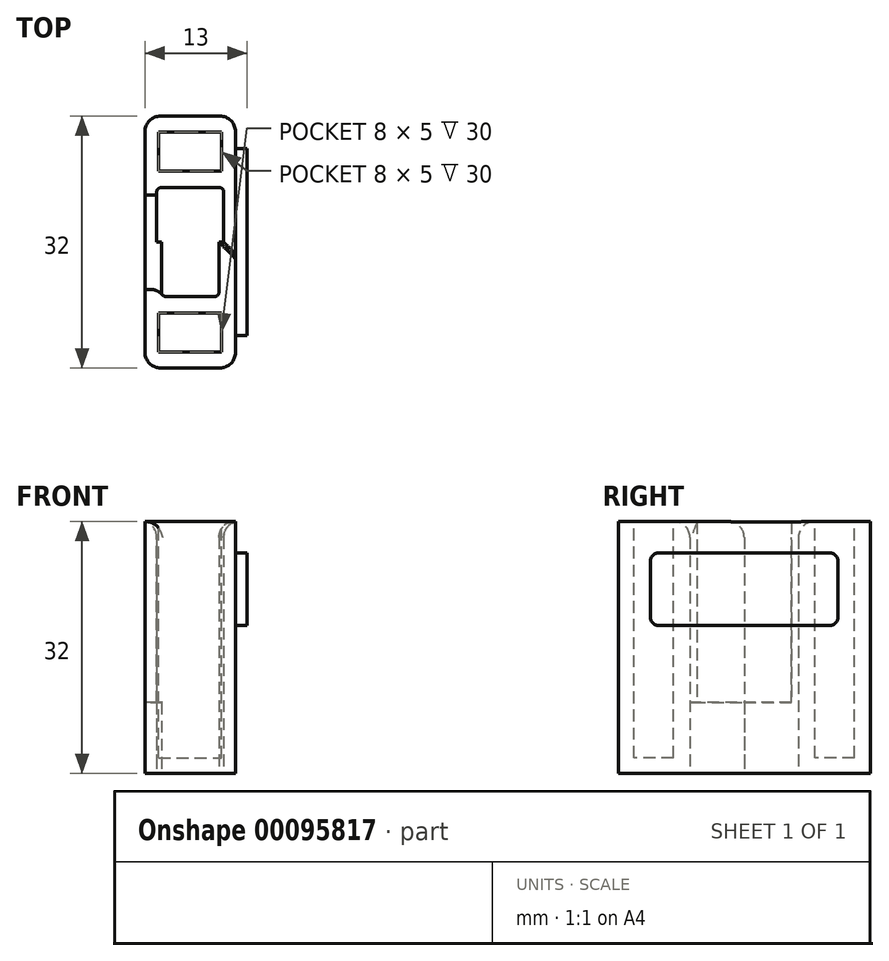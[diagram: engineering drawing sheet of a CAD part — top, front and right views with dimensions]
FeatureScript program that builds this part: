
annotation { "Feature Type Name" : "Feature", "Feature Type Description" : "" }
export const myFeature = defineFeature(function(context is Context, id is Id, definition is map)
    precondition{}
    {
        {
            var Q0;
            Q0=qCreatedBy(makeId("Top.planeOp"),FACE);
            var sketch = newSketch(context, id + "F0", { "sketchPlane" : qUnion([Q0])});
            skLineSegment(sketch, "E0.bottom", {"start": v(-3.75, 6.9) * mm, "end": v(3.75, 6.9) * mm});
            skLineSegment(sketch, "E0.left", {"start": v(-4.25, 6.4) * mm, "end": v(-4.25, 0) * mm});
            skLineSegment(sketch, "E0.right", {"start": v(4.25, 6.4) * mm, "end": v(4.25, 0) * mm});
            skLineSegment(sketch, "E1", {"start": v(-4.25, 0) * mm, "end": v(-3.65, 0) * mm});
            skLineSegment(sketch, "E2", {"start": v(-3.65, 0) * mm, "end": v(-3.65, -6.4) * mm});
            skLineSegment(sketch, "E3", {"start": v(4.25, 0) * mm, "end": v(3.65, 0) * mm});
            skLineSegment(sketch, "E4", {"start": v(3.65, 0) * mm, "end": v(3.65, -6.4) * mm});
            skLineSegment(sketch, "E5", {"start": v(-3.15, -6.9) * mm, "end": v(3.15, -6.9) * mm});
            skPoint(sketch, "E6.visualSharp", {"position": v(-4.25, 6.9) * mm});
            skArc(sketch, "E6.filletArc", {"start": v(-3.75, 6.9) * mm, "mid": v(-4.1, 6.75) * mm, "end": v(-4.25, 6.4) * mm});
            skPoint(sketch, "E7.visualSharp", {"position": v(4.25, 6.9) * mm});
            skArc(sketch, "E7.filletArc", {"start": v(4.25, 6.4) * mm, "mid": v(4.1, 6.75) * mm, "end": v(3.75, 6.9) * mm});
            skPoint(sketch, "E8.visualSharp", {"position": v(-3.65, -6.9) * mm});
            skArc(sketch, "E8.filletArc", {"start": v(-3.65, -6.4) * mm, "mid": v(-3.5, -6.75) * mm, "end": v(-3.15, -6.9) * mm});
            skPoint(sketch, "E9.visualSharp", {"position": v(3.65, -6.9) * mm});
            skArc(sketch, "E9.filletArc", {"start": v(3.15, -6.9) * mm, "mid": v(3.5, -6.75) * mm, "end": v(3.65, -6.4) * mm});
            skLineSegment(sketch, "E10.bottom", {"start": v(-5.75, 16) * mm, "end": v(5.75, 16) * mm});
            skLineSegment(sketch, "E10.top", {"start": v(-5.75, -16) * mm, "end": v(5.75, -16) * mm});
            skLineSegment(sketch, "E10.left", {"start": v(-5.75, 16) * mm, "end": v(-5.75, -16) * mm});
            skLineSegment(sketch, "E10.right", {"start": v(5.75, 16) * mm, "end": v(5.75, -16) * mm});
            skSolve(sketch);
        }
        {
            var Q0;
            Q0=makeQuery(id+"F0.imprint","IMPRINT",FACE,{"disambiguationData":[TD([[makeQuery(id+"F0.imprint","IMPRINT",EDGE,{"derivedFrom":sQuery(id+"F0.wireOp",EDGE,"E0.bottom")}),1.0]])]});
            extrude(context, id + "F1", {"entities" : qUnion([Q0]), "depth" : 32 * mm});
        }
        {
            var Q0;
            Q0=makeQuery(id+"F1.opExtrude","SWEPT_FACE",FACE,{"disambiguationData":[OSD([sQuery(id+"F0.wireOp",EDGE,"E10.right")])]});
            var sketch = newSketch(context, id + "F2", { "sketchPlane" : qUnion([Q0])});
            skLineSegment(sketch, "E11.bottom", {"start": v(-11.9, 28) * mm, "end": v(11.9, 28) * mm});
            skLineSegment(sketch, "E11.top", {"start": v(-11.9, 18.8) * mm, "end": v(11.9, 18.8) * mm});
            skLineSegment(sketch, "E11.left", {"start": v(-11.9, 28) * mm, "end": v(-11.9, 18.8) * mm});
            skLineSegment(sketch, "E11.right", {"start": v(11.9, 28) * mm, "end": v(11.9, 18.8) * mm});
            skSolve(sketch);
        }
        {
            var Q0;
            Q0=makeQuery(id+"F2.imprint","IMPRINT",FACE,{"disambiguationData":[TD([[makeQuery(id+"F2.imprint","IMPRINT",EDGE,{"derivedFrom":sQuery(id+"F2.wireOp",EDGE,"E11.bottom")}),-1.0]])]});
            extrude(context, id + "F3", {"entities" : qUnion([Q0]), "operationType" : NewBodyOperationType.ADD, "depth" : 1.5 * mm});
        }
        {
            var Q0;
            Q0=makeQuery(id+"F3.opExtrude","SWEPT_EDGE",EDGE,{"disambiguationData":[OSD([sQuery(id+"F2.wireOp",EDGE,"E11.top"),sQuery(id+"F2.wireOp",EDGE,"E11.left")])]});
            var Q1;
            Q1=makeQuery(id+"F3.opExtrude","SWEPT_EDGE",EDGE,{"disambiguationData":[OSD([sQuery(id+"F2.wireOp",EDGE,"E11.top"),sQuery(id+"F2.wireOp",EDGE,"E11.right")])]});
            var Q2;
            Q2=makeQuery(id+"F3.opExtrude","SWEPT_EDGE",EDGE,{"disambiguationData":[OSD([sQuery(id+"F2.wireOp",EDGE,"E11.bottom"),sQuery(id+"F2.wireOp",EDGE,"E11.right")])]});
            var Q3;
            Q3=makeQuery(id+"F3.opExtrude","SWEPT_EDGE",EDGE,{"disambiguationData":[OSD([sQuery(id+"F2.wireOp",EDGE,"E11.bottom"),sQuery(id+"F2.wireOp",EDGE,"E11.left")])]});
            fillet(context, id + "F4", {"entities" : qUnion([Q0, Q1, Q2, Q3]), "radius" : 1 * mm, "tangentPropagation" : true, "allowEdgeOverflow" : false});
        }
        {
            var Q0;
            Q0=makeQuery(id+"F1.opExtrude","SWEPT_FACE",FACE,{"disambiguationData":[OSD([sQuery(id+"F0.wireOp",EDGE,"E10.left")])]});
            var sketch = newSketch(context, id + "F5", { "sketchPlane" : qUnion([Q0])});
            skLineSegment(sketch, "E12.bottom", {"start": v(-6, 32) * mm, "end": v(6, 32) * mm});
            skLineSegment(sketch, "E12.top", {"start": v(-6, 9) * mm, "end": v(6, 9) * mm});
            skLineSegment(sketch, "E12.left", {"start": v(-6, 32) * mm, "end": v(-6, 9) * mm});
            skLineSegment(sketch, "E12.right", {"start": v(6, 32) * mm, "end": v(6, 9) * mm});
            skSolve(sketch);
        }
        {
            var Q0;
            Q0=makeQuery(id+"F5.imprint","IMPRINT",FACE,{"disambiguationData":[TD([[makeQuery(id+"F5.imprint","IMPRINT",EDGE,{"derivedFrom":sQuery(id+"F5.wireOp",EDGE,"E12.bottom")}),-1.0]])]});
            extrude(context, id + "F6", {"entities" : qUnion([Q0]), "operationType" : NewBodyOperationType.REMOVE, "oppositeDirection" : true, "depth" : 3 * mm});
        }
        {
            var Q0;
            Q0=makeQuery(id+"F1.opExtrude","CAP_FACE",FACE,{"disambiguationData":[OSD([sQuery(id+"F0.wireOp",EDGE,"E0.bottom"),sQuery(id+"F0.wireOp",EDGE,"E0.left"),sQuery(id+"F0.wireOp",EDGE,"E0.right"),sQuery(id+"F0.wireOp",EDGE,"E1"),sQuery(id+"F0.wireOp",EDGE,"E2"),sQuery(id+"F0.wireOp",EDGE,"E3"),sQuery(id+"F0.wireOp",EDGE,"E4"),sQuery(id+"F0.wireOp",EDGE,"E5"),sQuery(id+"F0.wireOp",EDGE,"E6.filletArc"),sQuery(id+"F0.wireOp",EDGE,"E7.filletArc"),sQuery(id+"F0.wireOp",EDGE,"E8.filletArc"),sQuery(id+"F0.wireOp",EDGE,"E9.filletArc"),sQuery(id+"F0.wireOp",EDGE,"E10.bottom"),sQuery(id+"F0.wireOp",EDGE,"E10.top"),sQuery(id+"F0.wireOp",EDGE,"E10.left"),sQuery(id+"F0.wireOp",EDGE,"E10.right")])],"isStart":false});
            var sketch = newSketch(context, id + "F7", { "sketchPlane" : qUnion([Q0])});
            skLineSegment(sketch, "E13.bottom", {"start": v(-4.02, 14) * mm, "end": v(3.98, 14) * mm});
            skLineSegment(sketch, "E13.top", {"start": v(-4.02, 9) * mm, "end": v(3.98, 9) * mm});
            skLineSegment(sketch, "E13.left", {"start": v(-4.02, 14) * mm, "end": v(-4.02, 9) * mm});
            skLineSegment(sketch, "E13.right", {"start": v(3.98, 14) * mm, "end": v(3.98, 9) * mm});
            skLineSegment(sketch, "E14.bottom", {"start": v(-4.02, -9) * mm, "end": v(3.98, -9) * mm});
            skLineSegment(sketch, "E14.top", {"start": v(-4.02, -14) * mm, "end": v(3.98, -14) * mm});
            skLineSegment(sketch, "E14.left", {"start": v(-4.02, -9) * mm, "end": v(-4.02, -14) * mm});
            skLineSegment(sketch, "E14.right", {"start": v(3.98, -9) * mm, "end": v(3.98, -14) * mm});
            skSolve(sketch);
        }
        {
            var Q0;
            Q0 = qSketchRegion(id + "F7", true);
            extrude(context, id + "F8", {"entities" : qUnion([Q0]), "operationType" : NewBodyOperationType.REMOVE, "oppositeDirection" : true, "depth" : 30 * mm});
        }
        {
            var Q0;
            Q0=makeQuery(id+"F1.opExtrude","SWEPT_EDGE",EDGE,{"disambiguationData":[OSD([sQuery(id+"F0.wireOp",EDGE,"E10.bottom"),sQuery(id+"F0.wireOp",EDGE,"E10.right")])]});
            var Q1;
            Q1=makeQuery(id+"F1.opExtrude","SWEPT_EDGE",EDGE,{"disambiguationData":[OSD([sQuery(id+"F0.wireOp",EDGE,"E10.bottom"),sQuery(id+"F0.wireOp",EDGE,"E10.left")])]});
            var Q2;
            Q2=makeQuery(id+"F1.opExtrude","CAP_EDGE",EDGE,{"disambiguationData":[OSD([sQuery(id+"F0.wireOp",EDGE,"E0.bottom")])],"isStart":false});
            var Q3;
            Q3=makeQuery(id+"F1.opExtrude","CAP_EDGE",EDGE,{"disambiguationData":[OSD([sQuery(id+"F0.wireOp",EDGE,"E3")])],"isStart":false});
            var Q4;
            Q4=makeQuery(id+"F1.opExtrude","CAP_EDGE",EDGE,{"disambiguationData":[OSD([sQuery(id+"F0.wireOp",EDGE,"E4")])],"isStart":false});
            var Q5;
            Q5=makeQuery(id+"F6.boolean.opBoolean","INTERSECT",EDGE,{"derivedFrom":[makeQuery(id+"F1.opExtrude","SWEPT_FACE",FACE,{"disambiguationData":[OSD([sQuery(id+"F0.wireOp",EDGE,"E2")])]}),makeQuery(id+"F6.opExtrude","SWEPT_FACE",FACE,{"disambiguationData":[OSD([sQuery(id+"F5.wireOp",EDGE,"E12.right")])]})]});
            var Q6;
            Q6=makeQuery(id+"F1.opExtrude","SWEPT_EDGE",EDGE,{"disambiguationData":[OSD([sQuery(id+"F0.wireOp",EDGE,"E10.top"),sQuery(id+"F0.wireOp",EDGE,"E10.right")])]});
            var Q7;
            Q7=makeQuery(id+"F1.opExtrude","SWEPT_EDGE",EDGE,{"disambiguationData":[OSD([sQuery(id+"F0.wireOp",EDGE,"E10.top"),sQuery(id+"F0.wireOp",EDGE,"E10.left")])]});
            fillet(context, id + "F9", {"entities" : qUnion([Q0, Q1, Q2, Q3, Q4, Q5, Q6, Q7]), "radius" : 2 * mm, "tangentPropagation" : true, "allowEdgeOverflow" : false});
        }
    });
